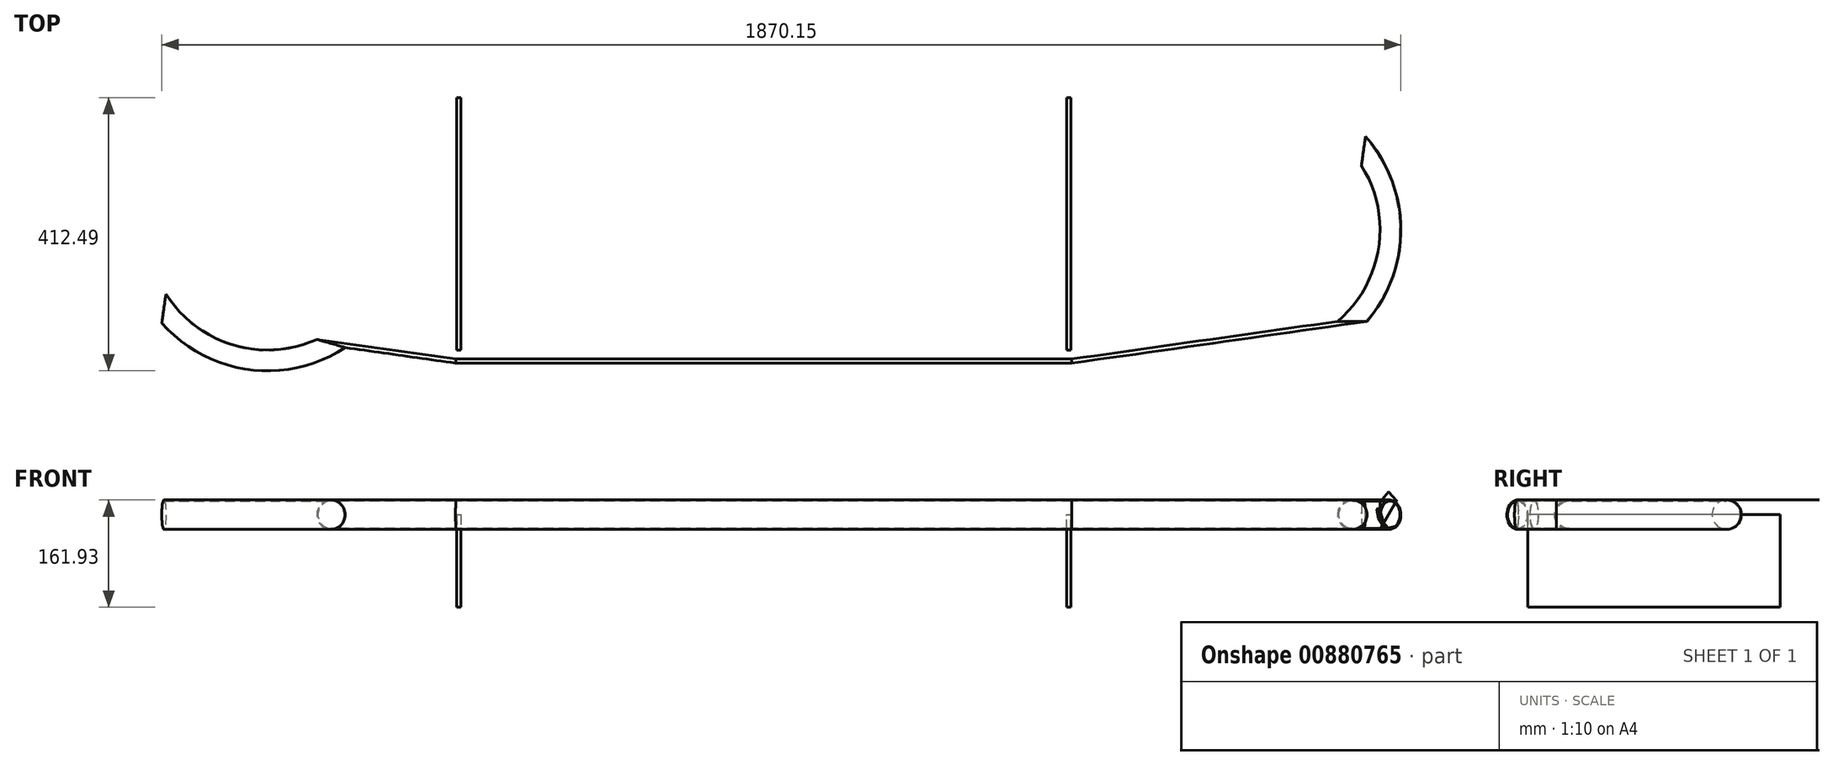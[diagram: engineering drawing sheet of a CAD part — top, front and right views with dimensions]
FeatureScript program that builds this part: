
annotation { "Feature Type Name" : "Feature", "Feature Type Description" : "" }
export const myFeature = defineFeature(function(context is Context, id is Id, definition is map)
    precondition{}
    {
        {
            var Q0;
            Q0=qCreatedBy(makeId("Front.planeOp"),FACE);
            var sketch = newSketch(context, id + "F0", { "sketchPlane" : qUnion([Q0])});
            skLineSegment(sketch, "E0.bottom", {"start": v(-44.95, 114.56) * mm, "end": v(-38.6, 114.56) * mm});
            skLineSegment(sketch, "E0.top", {"start": v(-44.95, -25.14) * mm, "end": v(-38.6, -25.14) * mm});
            skLineSegment(sketch, "E0.left", {"start": v(-44.95, 114.56) * mm, "end": v(-44.95, -25.14) * mm});
            skLineSegment(sketch, "E0.right", {"start": v(-38.6, 114.56) * mm, "end": v(-38.6, -25.14) * mm});
            skLineSegment(sketch, "E1.bottom", {"start": v(875.8, -25.14) * mm, "end": v(882.15, -25.14) * mm});
            skLineSegment(sketch, "E1.top", {"start": v(875.8, 114.56) * mm, "end": v(882.15, 114.56) * mm});
            skLineSegment(sketch, "E1.left", {"start": v(875.8, -25.14) * mm, "end": v(875.8, 114.56) * mm});
            skLineSegment(sketch, "E1.right", {"start": v(882.15, -25.14) * mm, "end": v(882.15, 114.56) * mm});
            skSolve(sketch);
        }
        {
            var Q0;
            Q0 = qSketchRegion(id + "F0", true);
            extrude(context, id + "F1", {"entities" : qUnion([Q0]), "oppositeDirection" : true, "depth" : 381 * mm, "offsetDistance" : 25.4 * mm});
        }
        {
            var Q0;
            Q0=makeQuery(id+"F1.opExtrude","CAP_VERTEX",VERTEX,{"disambiguationData":[OSD([sQuery(id+"F0.wireOp",EDGE,"E0.bottom"),sQuery(id+"F0.wireOp",EDGE,"E0.right")])],"isStart":false});
            var Q1;
            Q1=makeQuery(id+"F1.opExtrude","CAP_VERTEX",VERTEX,{"disambiguationData":[OSD([sQuery(id+"F0.wireOp",EDGE,"E0.bottom"),sQuery(id+"F0.wireOp",EDGE,"E0.right")])],"isStart":true});
            var Q2;
            Q2=makeQuery(id+"F1.opExtrude","CAP_VERTEX",VERTEX,{"disambiguationData":[OSD([sQuery(id+"F0.wireOp",EDGE,"E1.top"),sQuery(id+"F0.wireOp",EDGE,"E1.left")])],"isStart":true});
            cPlane(context, id + "F2", {"entities" : qUnion([Q0, Q1, Q2]), "cplaneType" : CPlaneType.THREE_POINT, "offset" : 25.4 * mm, "width" : 152.4 * mm, "height" : 152.4 * mm});
        }
        {
            var Q0;
            Q0=qCreatedBy(id+"F2.planeOp",FACE);
            var sketch = newSketch(context, id + "F3", { "sketchPlane" : qUnion([Q0])});
            skLineSegment(sketch, "E2", {"start": v(882.15, 0) * mm, "end": v(-44.95, 0) * mm});
            skLineSegment(sketch, "E3", {"start": v(-44.95, 0) * mm, "end": v(-349.75, -43.15) * mm});
            skLineSegment(sketch, "E4", {"start": v(418.6, 0) * mm, "end": v(418.6, -378.38) * mm});
            skArc(sketch, "E5", {"start": v(-349.75, -43.15) * mm, "mid": v(-435.65, -89.87) * mm, "end": v(-469.87, -181.47) * mm});
            skPoint(sketch, "E6.orphan", {"position": v(-469.53, -191.1) * mm});
            skLineSegment(sketch, "E7.MirrorCS", {"start": v(882.15, 0) * mm, "end": v(1186.95, -43.15) * mm});
            skArc(sketch, "E8.MirrorCS", {"start": v(1186.95, -43.15) * mm, "mid": v(1272.85, -89.87) * mm, "end": v(1307.07, -181.47) * mm});
            skLineSegment(sketch, "E9", {"start": v(1307.07, -181.47) * mm, "end": v(1307.07, 31.96) * mm});
            skSolve(sketch);
        }
        {
            var Q0;
            Q0=sQuery(id+"F3.wireOp",EDGE,"E9");
            var Q1;
            Q1=sQuery(id+"F3.wireOp",VERTEX,"E8.MirrorCS.end");
            cPlane(context, id + "F4", {"entities" : qUnion([Q0, Q1]), "cplaneType" : CPlaneType.LINE_POINT, "offset" : 25.4 * mm, "width" : 152.4 * mm, "height" : 152.4 * mm});
        }
        {
            var Q0;
            Q0=qCreatedBy(id+"F4.planeOp",FACE);
            var sketch = newSketch(context, id + "F5", { "sketchPlane" : qUnion([Q0])});
            skCircle(sketch, "E10", {"center": v(1307.07, 114.56) * mm, "radius": 20.7 * mm});
            skCircle(sketch, "E11", {"center": v(1307.07, 114.56) * mm, "radius": 22.23 * mm});
            skSolve(sketch);
        }
        {
            var Q0;
            Q0=makeQuery(id+"F5.imprint","IMPRINT",FACE,{"disambiguationData":[TD([[makeQuery(id+"F5.imprint","IMPRINT",EDGE,{"derivedFrom":sQuery(id+"F5.wireOp",EDGE,"E10")}),-1.0]])]});
            var Q1;
            Q1=sQuery(id+"F3.wireOp",EDGE,"E8.MirrorCS");
            var Q2;
            Q2=sQuery(id+"F3.wireOp",EDGE,"E7.MirrorCS");
            var Q3;
            Q3=sQuery(id+"F3.wireOp",EDGE,"E2");
            var Q4;
            Q4=sQuery(id+"F3.wireOp",EDGE,"E3");
            var Q5;
            Q5=sQuery(id+"F3.wireOp",EDGE,"E5");
            sweep(context, id + "F6", {"profiles" : qUnion([Q0]), "path" : qUnion([Q1, Q2, Q3, Q4, Q5])});
        }
    });
